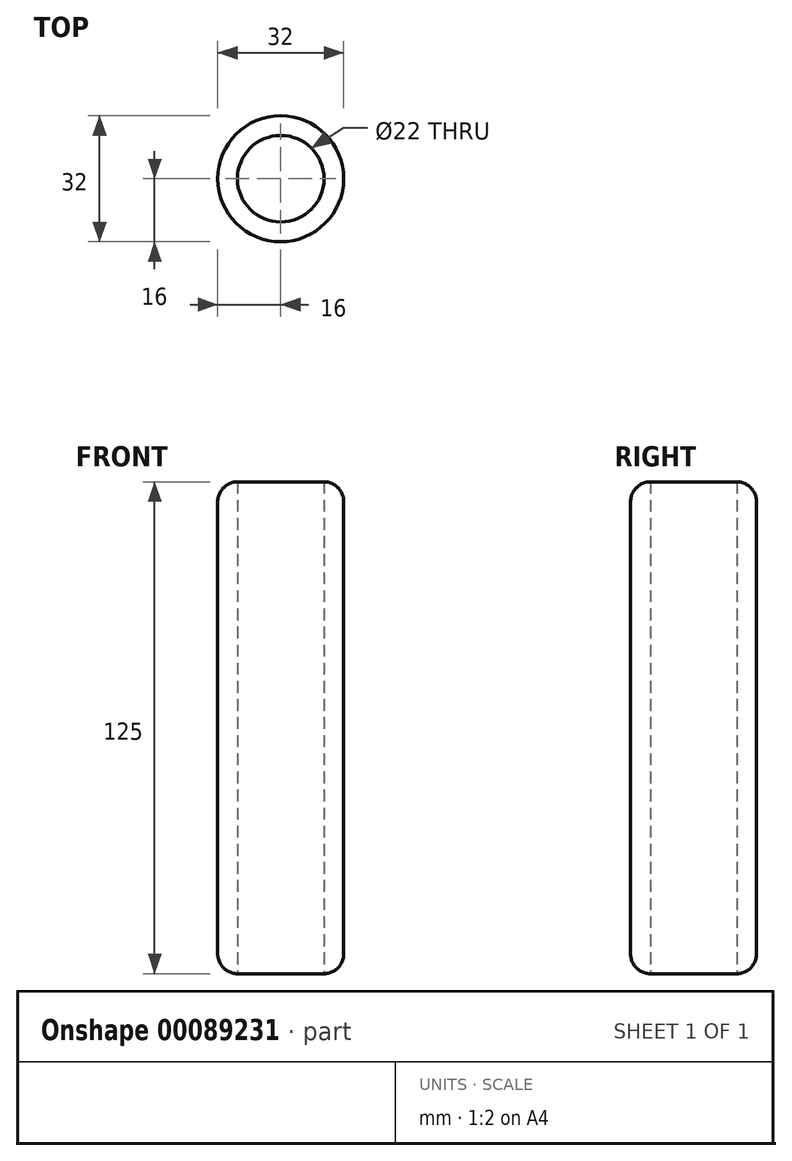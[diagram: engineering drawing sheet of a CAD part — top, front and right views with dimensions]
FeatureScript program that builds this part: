
annotation { "Feature Type Name" : "Feature", "Feature Type Description" : "" }
export const myFeature = defineFeature(function(context is Context, id is Id, definition is map)
    precondition{}
    {
        {
            var Q0;
            Q0=qCreatedBy(makeId("Top.planeOp"),FACE);
            var sketch = newSketch(context, id + "F0", { "sketchPlane" : qUnion([Q0])});
            skCircle(sketch, "E0", {"center": v(0, 0) * mm, "radius": 16 * mm});
            skCircle(sketch, "E1", {"center": v(0, 0) * mm, "radius": 11 * mm});
            skSolve(sketch);
        }
        {
            var Q0;
            Q0 = qSketchRegion(id + "F0", true);
            extrude(context, id + "F1", {"entities" : qUnion([Q0]), "depth" : 125 * mm});
        }
        {
            var Q0;
            Q0=makeQuery(id+"F1.opExtrude","CAP_EDGE",EDGE,{"disambiguationData":[OSD([sQuery(id+"F0.wireOp",EDGE,"E0")])],"isStart":false});
            fillet(context, id + "F2", {"entities" : qUnion([Q0]), "radius" : 5.08 * mm, "tangentPropagation" : true, "allowEdgeOverflow" : false});
        }
        {
            var Q0;
            Q0=makeQuery(id+"F1.opExtrude","CAP_EDGE",EDGE,{"disambiguationData":[OSD([sQuery(id+"F0.wireOp",EDGE,"E0")])],"isStart":true});
            fillet(context, id + "F3", {"entities" : qUnion([Q0]), "radius" : 5.08 * mm, "tangentPropagation" : true, "allowEdgeOverflow" : false});
        }
    });
